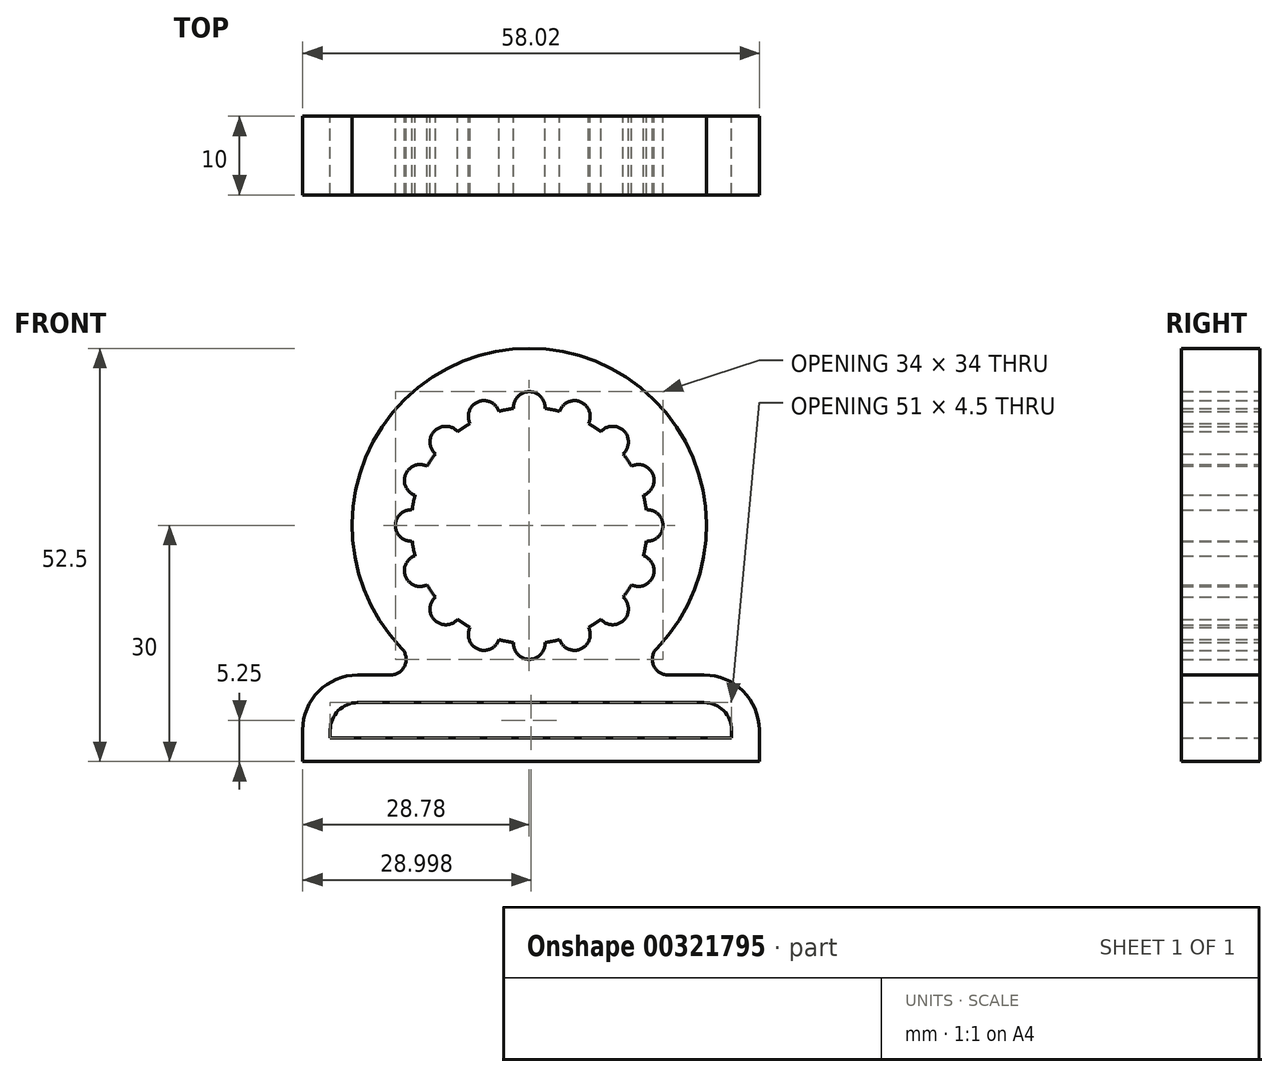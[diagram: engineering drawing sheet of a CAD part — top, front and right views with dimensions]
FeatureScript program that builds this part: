
annotation { "Feature Type Name" : "Feature", "Feature Type Description" : "" }
export const myFeature = defineFeature(function(context is Context, id is Id, definition is map)
    precondition{}
    {
        {
            var Q0;
            Q0=qCreatedBy(makeId("Front.planeOp"),FACE);
            var sketch = newSketch(context, id + "F0", { "sketchPlane" : qUnion([Q0])});
            skArc(sketch, "E0", {"start": v(-7.53, 12.97) * mm, "mid": v(-8.33, 12.47) * mm, "end": v(-9.1, 11.92) * mm});
            skArc(sketch, "E1", {"start": v(2, 14.87) * mm, "mid": v(0, 17) * mm, "end": v(-2, 14.87) * mm});
            skArc(sketch, "E2.1.0", {"start": v(-3.85, 14.5) * mm, "mid": v(-6.5, 15.7) * mm, "end": v(-7.53, 12.97) * mm});
            skArc(sketch, "E2.2.0", {"start": v(-9.1, 11.92) * mm, "mid": v(-12.02, 12.02) * mm, "end": v(-11.92, 9.1) * mm});
            skArc(sketch, "E2.3.0", {"start": v(-12.97, 7.53) * mm, "mid": v(-15.7, 6.5) * mm, "end": v(-14.5, 3.85) * mm});
            skArc(sketch, "E2.4.0", {"start": v(-14.87, 2) * mm, "mid": v(-17, 0) * mm, "end": v(-14.87, -2) * mm});
            skArc(sketch, "E2.5.0", {"start": v(-14.5, -3.85) * mm, "mid": v(-15.7, -6.5) * mm, "end": v(-12.97, -7.53) * mm});
            skArc(sketch, "E2.6.0", {"start": v(-11.92, -9.1) * mm, "mid": v(-12.02, -12.02) * mm, "end": v(-9.1, -11.92) * mm});
            skArc(sketch, "E2.7.0", {"start": v(-7.53, -12.97) * mm, "mid": v(-6.5, -15.7) * mm, "end": v(-3.85, -14.5) * mm});
            skArc(sketch, "E2.8.0", {"start": v(-2, -14.87) * mm, "mid": v(0, -17) * mm, "end": v(2, -14.87) * mm});
            skArc(sketch, "E2.9.0", {"start": v(3.85, -14.5) * mm, "mid": v(6.5, -15.7) * mm, "end": v(7.53, -12.97) * mm});
            skArc(sketch, "E2.10.0", {"start": v(9.1, -11.92) * mm, "mid": v(12.02, -12.02) * mm, "end": v(11.92, -9.1) * mm});
            skArc(sketch, "E2.11.0", {"start": v(12.97, -7.53) * mm, "mid": v(15.7, -6.5) * mm, "end": v(14.5, -3.85) * mm});
            skArc(sketch, "E2.12.0", {"start": v(14.87, -2) * mm, "mid": v(17, 0) * mm, "end": v(14.87, 2) * mm});
            skArc(sketch, "E2.13.0", {"start": v(14.5, 3.85) * mm, "mid": v(15.7, 6.5) * mm, "end": v(12.97, 7.53) * mm});
            skArc(sketch, "E2.14.0", {"start": v(11.92, 9.1) * mm, "mid": v(12.02, 12.02) * mm, "end": v(9.1, 11.92) * mm});
            skArc(sketch, "E2.15.0", {"start": v(7.53, 12.97) * mm, "mid": v(6.5, 15.7) * mm, "end": v(3.85, 14.5) * mm});
            skArc(sketch, "E3", {"start": v(16.2, -15.61) * mm, "mid": v(0, 22.5) * mm, "end": v(-16.2, -15.61) * mm});
            skArc(sketch, "E4.trimOffspring", {"start": v(-2, 14.87) * mm, "mid": v(-2.93, 14.71) * mm, "end": v(-3.85, 14.5) * mm});
            skArc(sketch, "E5.trimOffspring", {"start": v(3.85, 14.5) * mm, "mid": v(2.93, 14.71) * mm, "end": v(2, 14.87) * mm});
            skArc(sketch, "E6.trimOffspring", {"start": v(9.1, 11.92) * mm, "mid": v(8.33, 12.47) * mm, "end": v(7.53, 12.97) * mm});
            skArc(sketch, "E7.trimOffspring", {"start": v(12.97, 7.53) * mm, "mid": v(12.47, 8.33) * mm, "end": v(11.92, 9.1) * mm});
            skArc(sketch, "E8.trimOffspring", {"start": v(14.87, 2) * mm, "mid": v(14.71, 2.93) * mm, "end": v(14.5, 3.85) * mm});
            skArc(sketch, "E9.trimOffspring", {"start": v(14.5, -3.85) * mm, "mid": v(14.71, -2.93) * mm, "end": v(14.87, -2) * mm});
            skArc(sketch, "E10.trimOffspring", {"start": v(11.92, -9.1) * mm, "mid": v(12.47, -8.33) * mm, "end": v(12.97, -7.53) * mm});
            skArc(sketch, "E11.trimOffspring", {"start": v(7.53, -12.97) * mm, "mid": v(8.33, -12.47) * mm, "end": v(9.1, -11.92) * mm});
            skArc(sketch, "E12.trimOffspring", {"start": v(2, -14.87) * mm, "mid": v(2.93, -14.71) * mm, "end": v(3.85, -14.5) * mm});
            skArc(sketch, "E13.trimOffspring", {"start": v(-3.85, -14.5) * mm, "mid": v(-2.93, -14.71) * mm, "end": v(-2, -14.87) * mm});
            skArc(sketch, "E14.trimOffspring", {"start": v(-9.1, -11.92) * mm, "mid": v(-8.33, -12.47) * mm, "end": v(-7.53, -12.97) * mm});
            skArc(sketch, "E15.trimOffspring", {"start": v(-12.97, -7.53) * mm, "mid": v(-12.47, -8.33) * mm, "end": v(-11.92, -9.1) * mm});
            skArc(sketch, "E16.trimOffspring", {"start": v(-14.87, -2) * mm, "mid": v(-14.71, -2.93) * mm, "end": v(-14.5, -3.85) * mm});
            skArc(sketch, "E17.trimOffspring", {"start": v(-14.5, 3.85) * mm, "mid": v(-14.71, 2.93) * mm, "end": v(-14.87, 2) * mm});
            skArc(sketch, "E18.trimOffspring", {"start": v(-11.92, 9.1) * mm, "mid": v(-12.47, 8.33) * mm, "end": v(-12.97, 7.53) * mm});
            skPoint(sketch, "E19.endSnap0", {"position": v(-17, 0) * mm});
            skLineSegment(sketch, "E20.0", {"start": v(-28.78, -30) * mm, "end": v(29.24, -30) * mm});
            skLineSegment(sketch, "E21.0", {"start": v(-21.78, -19) * mm, "end": v(-17.64, -19) * mm});
            skArc(sketch, "E22", {"start": v(-17.64, -19) * mm, "mid": v(-15.8, -17.78) * mm, "end": v(-16.2, -15.61) * mm});
            skArc(sketch, "E23.1.0.0", {"start": v(16.2, -15.61) * mm, "mid": v(15.8, -17.78) * mm, "end": v(17.64, -19) * mm});
            skLineSegment(sketch, "E24.0", {"start": v(-25.28, -27) * mm, "end": v(25.72, -27) * mm});
            skArc(sketch, "E25", {"start": v(-21.78, -19) * mm, "mid": v(-26.73, -21.05) * mm, "end": v(-28.78, -26) * mm});
            skArc(sketch, "E26", {"start": v(-21.78, -22.5) * mm, "mid": v(-24.26, -23.53) * mm, "end": v(-25.28, -26) * mm});
            skArc(sketch, "E27.1.0.0", {"start": v(29.22, -25.97) * mm, "mid": v(27.16, -21.04) * mm, "end": v(22.22, -19) * mm});
            skArc(sketch, "E27.1.0.1", {"start": v(25.72, -26) * mm, "mid": v(24.7, -23.53) * mm, "end": v(22.22, -22.5) * mm});
            skLineSegment(sketch, "E28.trimOffspring", {"start": v(17.64, -19) * mm, "end": v(22.22, -19) * mm});
            skLineSegment(sketch, "E29", {"start": v(-28.78, -26) * mm, "end": v(-28.78, -30.08) * mm});
            skLineSegment(sketch, "E30", {"start": v(-25.28, -26) * mm, "end": v(-25.28, -27) * mm});
            skLineSegment(sketch, "E31", {"start": v(25.72, -26) * mm, "end": v(25.72, -27) * mm});
            skLineSegment(sketch, "E32", {"start": v(29.22, -25.97) * mm, "end": v(29.24, -30) * mm});
            skLineSegment(sketch, "E33", {"start": v(-21.78, -22.5) * mm, "end": v(22.22, -22.5) * mm});
            skSolve(sketch);
        }
        {
            var Q0;
            Q0=makeQuery(id+"F0.imprint","IMPRINT",FACE,{"disambiguationData":[TD([[makeQuery(id+"F0.imprint","IMPRINT",EDGE,{"derivedFrom":sQuery(id+"F0.wireOp",EDGE,"E0")}),-1.0]])]});
            extrude(context, id + "F1", {"entities" : qUnion([Q0]), "endBound" : BoundingType.SYMMETRIC, "depth" : 10 * mm});
        }
    });
